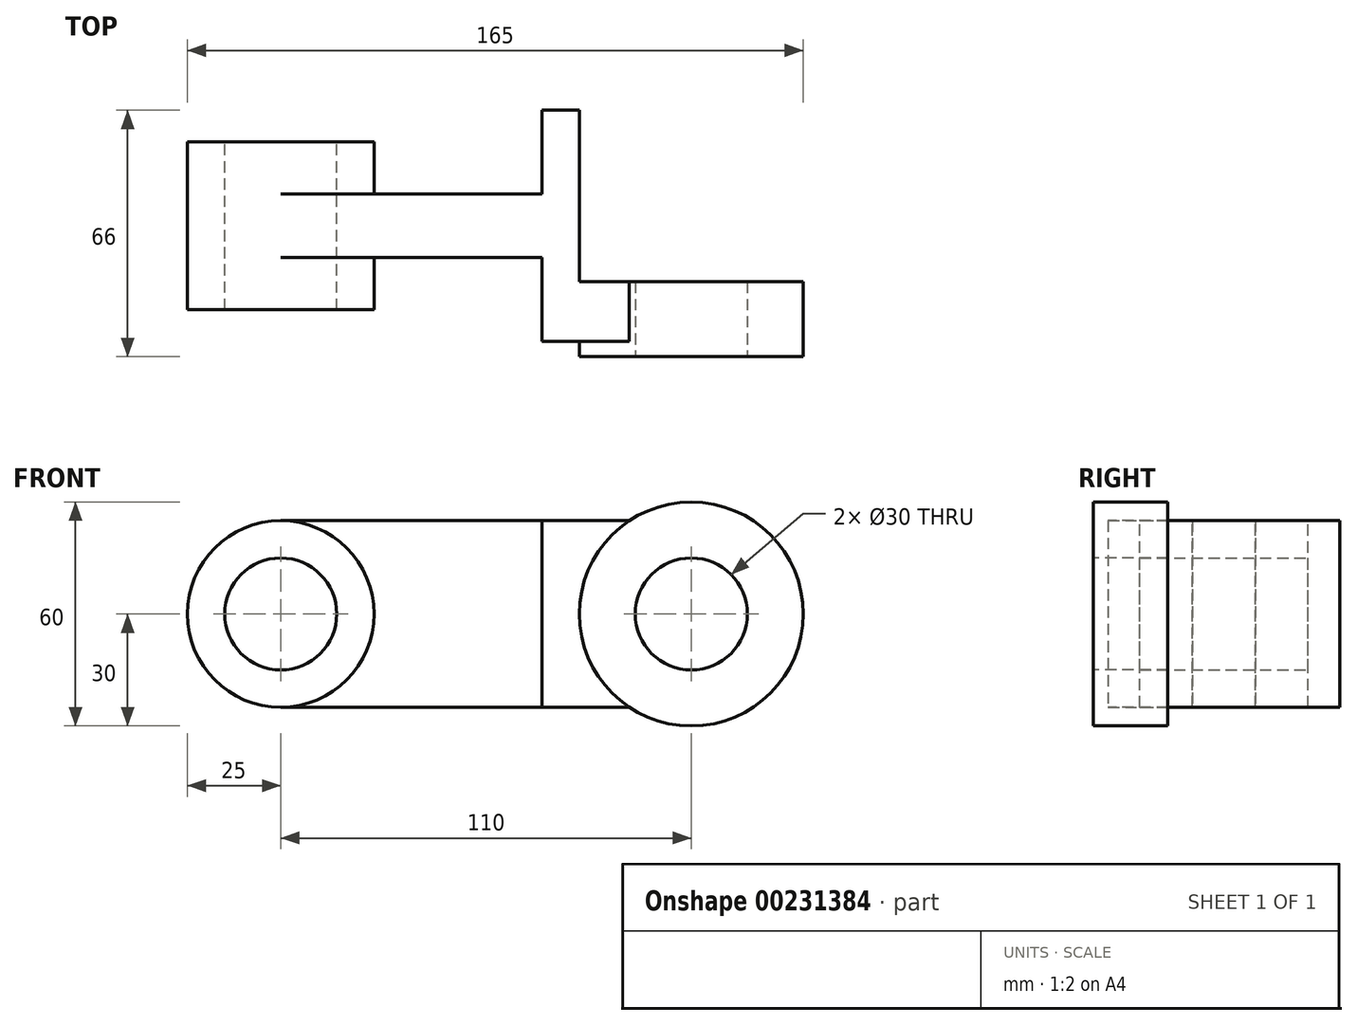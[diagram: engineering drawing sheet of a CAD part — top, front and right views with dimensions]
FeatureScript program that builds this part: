
annotation { "Feature Type Name" : "Feature", "Feature Type Description" : "" }
export const myFeature = defineFeature(function(context is Context, id is Id, definition is map)
    precondition{}
    {
        {
            var Q0;
            Q0=qCreatedBy(makeId("Front.planeOp"),FACE);
            var sketch = newSketch(context, id + "F0", { "sketchPlane" : qUnion([Q0])});
            skCircle(sketch, "E0", {"center": v(0, 0) * mm, "radius": 25 * mm});
            skCircle(sketch, "E1", {"center": v(0, 0) * mm, "radius": 15 * mm});
            skLineSegment(sketch, "E2", {"start": v(0, 25) * mm, "end": v(70, 25) * mm});
            skLineSegment(sketch, "E3", {"start": v(70, 25) * mm, "end": v(70, -25) * mm});
            skLineSegment(sketch, "E4", {"start": v(70, -25) * mm, "end": v(0, -25) * mm});
            skSolve(sketch);
        }
        {
            var Q0;
            Q0=makeQuery(id+"F0.imprint","IMPRINT",FACE,{"disambiguationData":[TD([[makeQuery(id+"F0.imprint","IMPRINT",EDGE,{"derivedFrom":sQuery(id+"F0.wireOp",EDGE,"E1")}),-1.0]])]});
            extrude(context, id + "F1", {"entities" : qUnion([Q0]), "endBound" : BoundingType.SYMMETRIC, "depth" : 45 * mm});
        }
        {
            var Q0;
            {var subQ0=sQuery(id+"F0.wireOp",EDGE,"E2");Q0=makeQuery(id+"F0.imprint","IMPRINT",FACE,{"disambiguationData":[TD([[makeQuery(id+"F0.imprint","IMPRINT",EDGE,{"derivedFrom":subQ0}),-1.0]])]});}
            extrude(context, id + "F2", {"entities" : qUnion([Q0]), "operationType" : NewBodyOperationType.ADD, "endBound" : BoundingType.SYMMETRIC, "depth" : 17 * mm});
        }
        {
            var Q0;
            Q0=qCreatedBy(makeId("Front.planeOp"),FACE);
            var sketch = newSketch(context, id + "F3", { "sketchPlane" : qUnion([Q0])});
            skLineSegment(sketch, "E5", {"start": v(70, 25) * mm, "end": v(80, 25) * mm});
            skLineSegment(sketch, "E6", {"start": v(80, 25) * mm, "end": v(80, -25) * mm});
            skLineSegment(sketch, "E7", {"start": v(80, -25) * mm, "end": v(70, -25) * mm});
            skSolve(sketch);
        }
        {
            var Q0;
            Q0=qCreatedBy(makeId("Front.planeOp"),FACE);
            var sketch = newSketch(context, id + "F4", { "sketchPlane" : qUnion([Q0])});
            skPoint(sketch, "E8.0", {"position": v(75, 25) * mm});
            skLineSegment(sketch, "E9.0", {"start": v(70, 25) * mm, "end": v(80, 25) * mm});
            skLineSegment(sketch, "E10.0", {"start": v(80, 25) * mm, "end": v(80, -25) * mm});
            skLineSegment(sketch, "E11.0", {"start": v(80, -25) * mm, "end": v(70, -25) * mm});
            skSolve(sketch);
        }
        {
            var Q0;
            Q0=qCreatedBy(makeId("Front.planeOp"),FACE);
            var sketch = newSketch(context, id + "F5", { "sketchPlane" : qUnion([Q0])});
            skLineSegment(sketch, "E12.0", {"start": v(70, 25) * mm, "end": v(80, 25) * mm});
            skLineSegment(sketch, "E13.0", {"start": v(70, 25) * mm, "end": v(70, -25) * mm});
            skLineSegment(sketch, "E14.0", {"start": v(80, 25) * mm, "end": v(80, -25) * mm});
            skPoint(sketch, "E15.0", {"position": v(75, -25) * mm});
            skLineSegment(sketch, "E16.0", {"start": v(80, -25) * mm, "end": v(70, -25) * mm});
            skSolve(sketch);
        }
        {
            var Q0;
            Q0=makeQuery(id+"F5.imprint","IMPRINT",FACE,{"disambiguationData":[TD([[makeQuery(id+"F5.imprint","IMPRINT",EDGE,{"derivedFrom":sQuery(id+"F5.wireOp",EDGE,"E12.0")}),-1.0]])]});
            extrude(context, id + "F6", {"entities" : qUnion([Q0]), "operationType" : NewBodyOperationType.ADD, "endBound" : BoundingType.SYMMETRIC, "depth" : 62 * mm});
        }
        {
            var Q0;
            Q0=makeQuery(id+"F6.opExtrude","CAP_FACE",FACE,{"disambiguationData":[OSD([sQuery(id+"F5.wireOp",EDGE,"E12.0"),sQuery(id+"F5.wireOp",EDGE,"E13.0"),sQuery(id+"F5.wireOp",EDGE,"E14.0"),sQuery(id+"F5.wireOp",EDGE,"E16.0")])],"isStart":false});
            var sketch = newSketch(context, id + "F7", { "sketchPlane" : qUnion([Q0])});
            skSolve(sketch);
        }
        {
            var Q0;
            Q0=makeQuery(id+"F7.imprint","IMPRINT",FACE,{"disambiguationData":[TD([[makeQuery(id+"F7.imprint","IMPRINT",EDGE,{"derivedFrom":makeQuery(id+"F6.opExtrude","CAP_EDGE",EDGE,{"disambiguationData":[OSD([sQuery(id+"F5.wireOp",EDGE,"E12.0")])],"isStart":false})}),-1.0]])]});
            var sketch = newSketch(context, id + "F8", { "sketchPlane" : qUnion([Q0])});
            skLineSegment(sketch, "E17.0", {"start": v(70, 25) * mm, "end": v(80, 25) * mm});
            skLineSegment(sketch, "E18.0", {"start": v(70, 25) * mm, "end": v(70, -25) * mm});
            skLineSegment(sketch, "E19.0", {"start": v(80, 25) * mm, "end": v(80, -25) * mm});
            skPoint(sketch, "E20.0", {"position": v(75, -25) * mm});
            skLineSegment(sketch, "E21", {"start": v(80, 25) * mm, "end": v(93.42, 25) * mm});
            skLineSegment(sketch, "E22", {"start": v(80, -25) * mm, "end": v(93.42, -25) * mm});
            skCircle(sketch, "E23", {"center": v(110, 0) * mm, "radius": 30 * mm});
            skCircle(sketch, "E24", {"center": v(110, 0) * mm, "radius": 15 * mm});
            skSolve(sketch);
        }
        {
            var Q0;
            {var subQ0=sQuery(id+"F8.wireOp",EDGE,"E21");Q0=makeQuery(id+"F8.imprint","IMPRINT",FACE,{"disambiguationData":[TD([[makeQuery(id+"F8.imprint","IMPRINT",EDGE,{"derivedFrom":subQ0}),-1.0]])]});}
            var Q1;
            Q1=makeQuery(id+"F8.imprint","IMPRINT",FACE,{"disambiguationData":[TD([[makeQuery(id+"F8.imprint","IMPRINT",EDGE,{"derivedFrom":sQuery(id+"F8.wireOp",EDGE,"E24")}),-1.0]])]});
            var Q2;
            {var subQ0=sQuery(id+"F8.wireOp",EDGE,"E22");Q2=makeQuery(id+"F8.imprint","IMPRINT",FACE,{"disambiguationData":[TD([[makeQuery(id+"F8.imprint","IMPRINT",EDGE,{"derivedFrom":subQ0}),1.0]])]});}
            extrude(context, id + "F9", {"entities" : qUnion([Q0, Q1, Q2]), "operationType" : NewBodyOperationType.ADD, "oppositeDirection" : true, "depth" : 16 * mm});
        }
        {
            var Q0;
            Q0=qSketchRegion(id+"F8",true);
            extrude(context, id + "F10", {"entities" : qUnion([Q0]), "operationType" : NewBodyOperationType.ADD, "oppositeDirection" : true, "depth" : 14 * mm});
        }
        {
            var Q0;
            Q0=makeQuery(id+"F8.imprint","IMPRINT",FACE,{"disambiguationData":[TD([[makeQuery(id+"F8.imprint","IMPRINT",EDGE,{"derivedFrom":sQuery(id+"F8.wireOp",EDGE,"E24")}),-1.0]])]});
            cPlane(context, id + "F11", {"entities" : qUnion([Q0]), "cplaneType" : CPlaneType.OFFSET, "offset" : 0 * mm, "width" : 150 * mm, "height" : 150 * mm});
        }
        {
            var Q0;
            Q0=makeQuery(id+"F8.imprint","IMPRINT",FACE,{"disambiguationData":[TD([[makeQuery(id+"F8.imprint","IMPRINT",EDGE,{"derivedFrom":sQuery(id+"F8.wireOp",EDGE,"E24")}),-1.0]])]});
            extrude(context, id + "F12", {"entities" : qUnion([Q0]), "operationType" : NewBodyOperationType.ADD, "depth" : 4 * mm});
        }
    });
